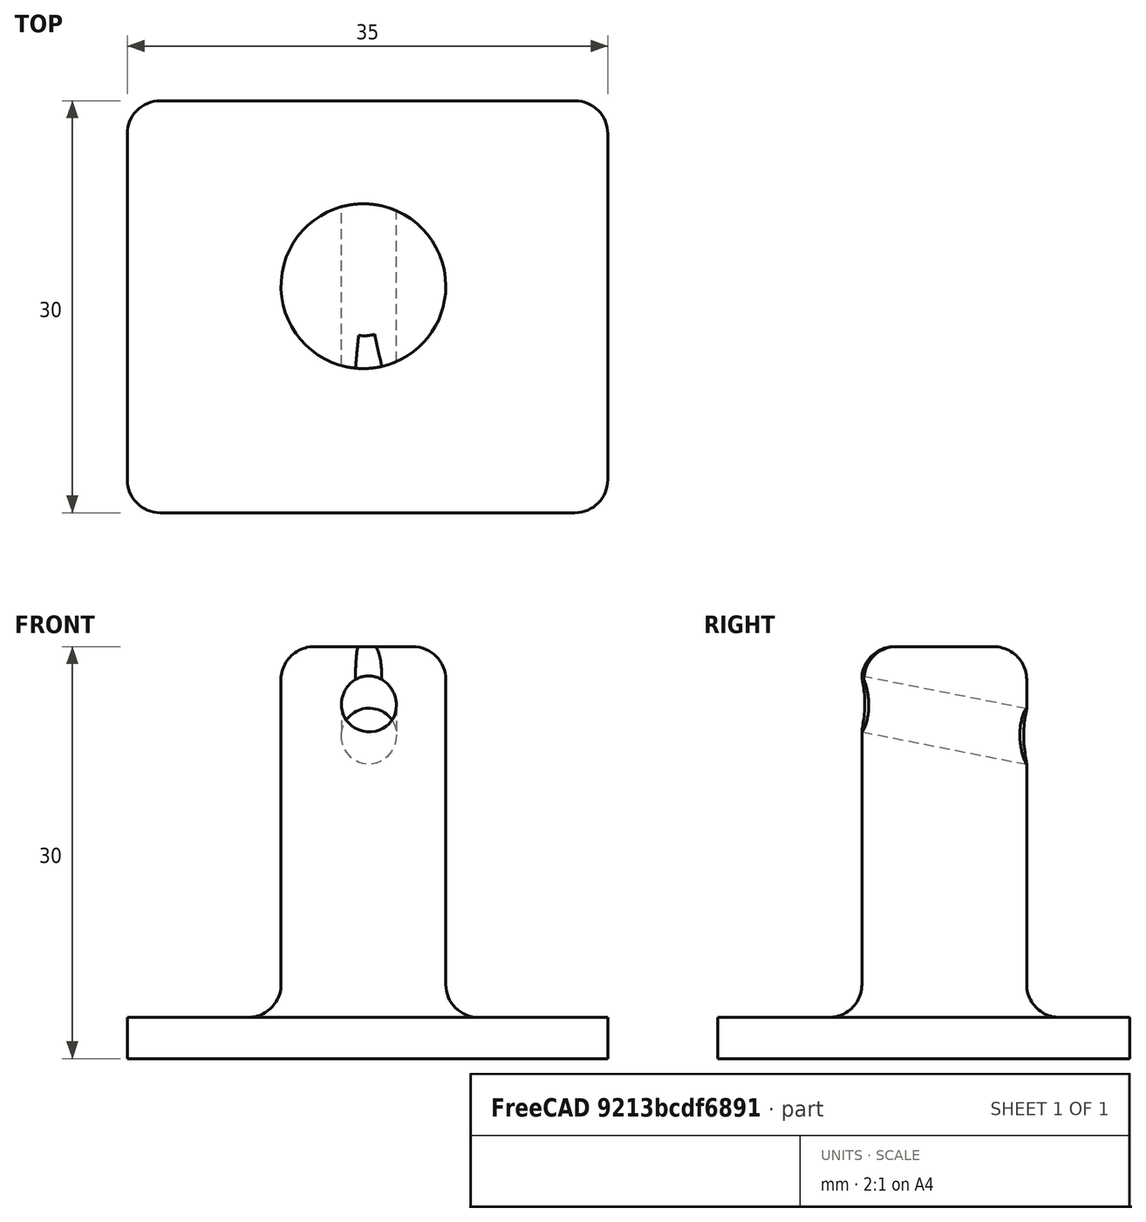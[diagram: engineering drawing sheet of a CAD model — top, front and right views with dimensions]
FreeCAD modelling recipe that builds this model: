
FCSTD DOCUMENT  (FreeCAD 0.19R24267 +99 (Git))
Label: 出si导管
License: All rights reserved
LicenseURL: http://en.wikipedia.org/wiki/All_rights_reserved
objects: Part::Cylinder×2, Part::Fillet×2, Part::Box×1, Part::MultiFuse×1, Part::Cut×1
note: 7 computed .brp shape members not serialized (recipe doc carries the construction recipe); baked Part::Feature solids carry a one-line shape summary decoded from their .brp

FEATURE [Part::Box] Box  label="立方体"
  AttacherType = Attacher::AttachEngine3D
  Height = 3
  Length = 35
  Width = 30
FEATURE [Part::Cylinder] Cylinder  label="圆柱体"
  Angle = 360
  AttacherType = Attacher::AttachEngine3D
  Height = 30
  Placement = pos=(17.2,16.5,0) rot=(0,0,1;0rad)
  Radius = 6
FEATURE [Part::Cylinder] Cylinder001  label="圆柱体001"
  Angle = 360
  AttacherType = Attacher::AttachEngine3D
  Height = 25
  Placement = pos=(17.6,6.7699,26.5629) rot=(-1,0,0;1.76453rad)
  Radius = 2
FEATURE [Part::MultiFuse] Fusion
  Shapes = -> [Cylinder,Box]
FEATURE [Part::Cut] Cut
  Base = -> Fusion
  Tool = -> Cylinder001
FEATURE [Part::Fillet] Fillet
  Base = -> Cut
  Edges = 1 edges r=2.4: [Edge1]
FEATURE [Part::Fillet] Fillet001
  Base = -> Fillet
  Edges = 5 edges r=2.4: [Edge3,Edge13,Edge14,Edge17,Edge19]
